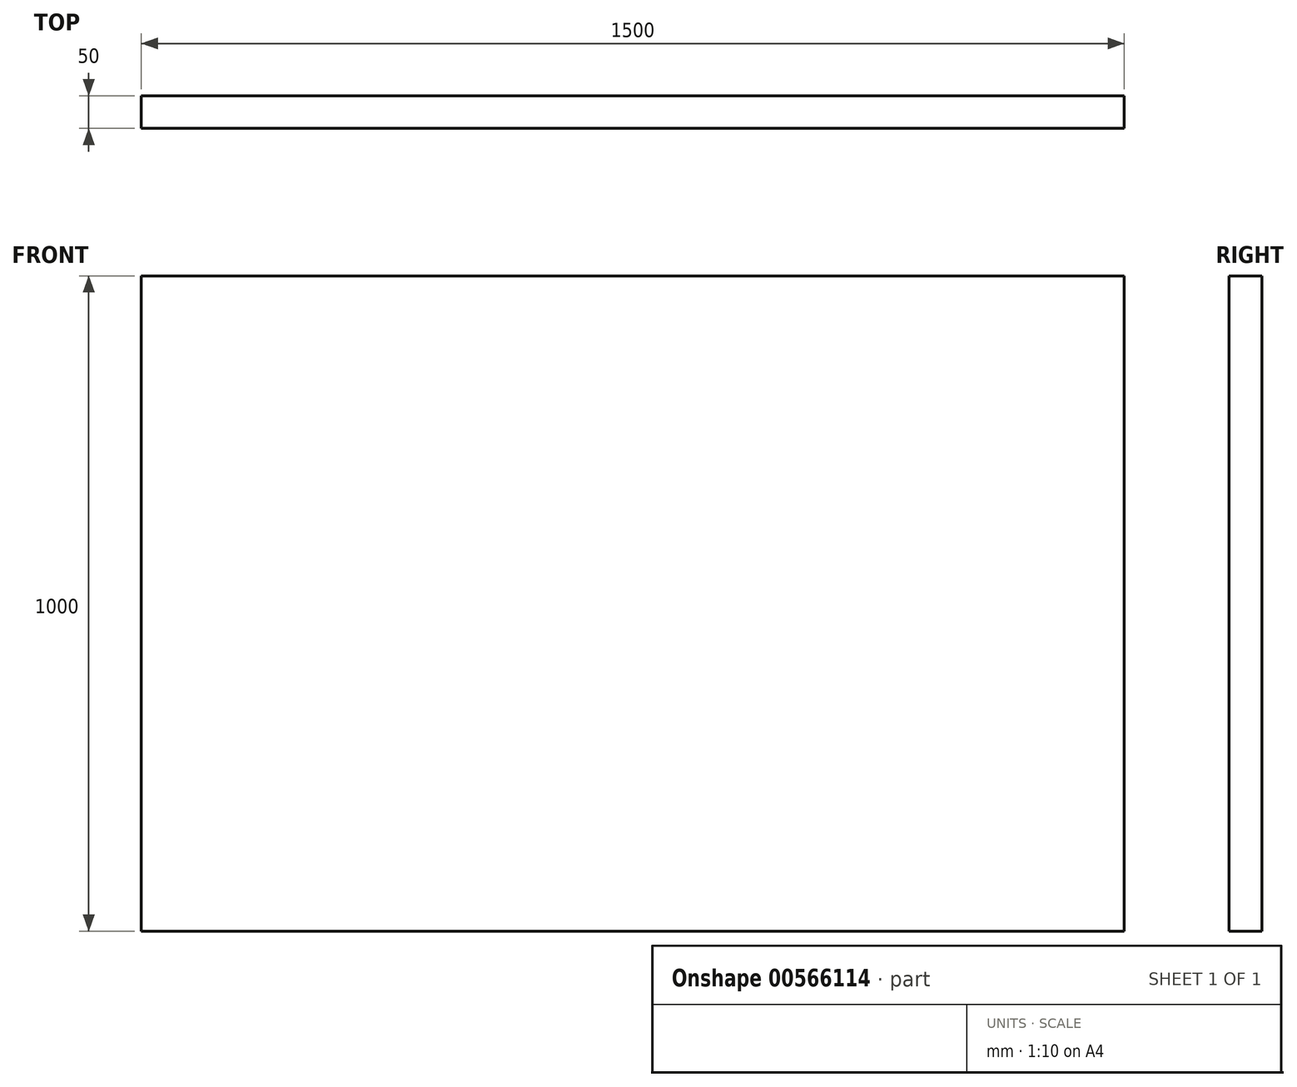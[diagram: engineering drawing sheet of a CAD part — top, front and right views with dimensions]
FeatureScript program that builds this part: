
annotation { "Feature Type Name" : "Feature", "Feature Type Description" : "" }
export const myFeature = defineFeature(function(context is Context, id is Id, definition is map)
    precondition{}
    {
        {
            var Q0;
            Q0=qCreatedBy(makeId("Front.planeOp"),FACE);
            var sketch = newSketch(context, id + "F0", { "sketchPlane" : qUnion([Q0])});
            skLineSegment(sketch, "E0.bottom", {"start": v(1406, -19.26) * mm, "end": v(-94, -19.26) * mm});
            skLineSegment(sketch, "E0.top", {"start": v(1406, 980.74) * mm, "end": v(-94, 980.74) * mm});
            skLineSegment(sketch, "E0.left", {"start": v(1406, -19.26) * mm, "end": v(1406, 980.74) * mm});
            skLineSegment(sketch, "E0.right", {"start": v(-94, -19.26) * mm, "end": v(-94, 980.74) * mm});
            skPoint(sketch, "E0.middle", {"position": v(656, 480.74) * mm});
            skSolve(sketch);
        }
        {
            var Q0;
            Q0 = qSketchRegion(id + "F0", true);
            extrude(context, id + "F1", {"entities" : qUnion([Q0]), "depth" : 50 * mm, "offsetDistance" : 25 * mm});
        }
    });
